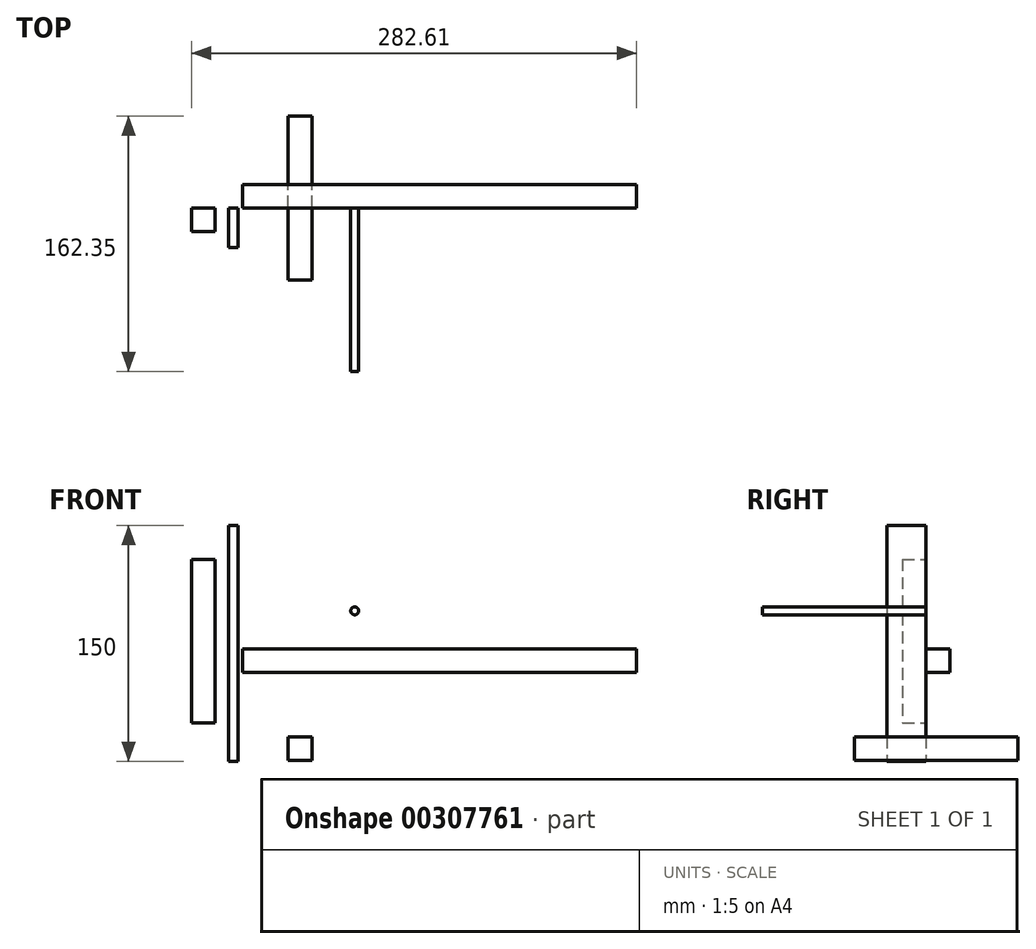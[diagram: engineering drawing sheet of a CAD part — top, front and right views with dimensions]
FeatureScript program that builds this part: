
annotation { "Feature Type Name" : "Feature", "Feature Type Description" : "" }
export const myFeature = defineFeature(function(context is Context, id is Id, definition is map)
    precondition{}
    {
        {
            var Q0;
            Q0=qCreatedBy(makeId("Top.planeOp"),FACE);
            var sketch = newSketch(context, id + "F0", { "sketchPlane" : qUnion([Q0])});
            skLineSegment(sketch, "E0.bottom", {"start": v(-28.87, 15) * mm, "end": v(221.13, 15) * mm});
            skLineSegment(sketch, "E0.top", {"start": v(-28.87, 0) * mm, "end": v(221.13, 0) * mm});
            skLineSegment(sketch, "E0.left", {"start": v(-28.87, 15) * mm, "end": v(-28.87, 0) * mm});
            skLineSegment(sketch, "E0.right", {"start": v(221.13, 15) * mm, "end": v(221.13, 0) * mm});
            skSolve(sketch);
        }
        {
            var Q0;
            Q0 = qSketchRegion(id + "F0", true);
            extrude(context, id + "F1", {"entities" : qUnion([Q0]), "depth" : 15 * mm});
        }
        {
            var Q0;
            Q0=qCreatedBy(makeId("Right.planeOp"),FACE);
            var sketch = newSketch(context, id + "F2", { "sketchPlane" : qUnion([Q0])});
            skLineSegment(sketch, "E1.bottom", {"start": v(-45.65, -40.85) * mm, "end": v(58.35, -40.85) * mm});
            skLineSegment(sketch, "E1.top", {"start": v(-45.65, -55.85) * mm, "end": v(58.35, -55.85) * mm});
            skLineSegment(sketch, "E1.left", {"start": v(-45.65, -40.85) * mm, "end": v(-45.65, -55.85) * mm});
            skLineSegment(sketch, "E1.right", {"start": v(58.35, -40.85) * mm, "end": v(58.35, -55.85) * mm});
            skSolve(sketch);
        }
        {
            var Q0;
            Q0 = qSketchRegion(id + "F2", true);
            extrude(context, id + "F3", {"entities" : qUnion([Q0]), "depth" : 15 * mm});
        }
        {
            var Q0;
            Q0=qCreatedBy(makeId("Front.planeOp"),FACE);
            var sketch = newSketch(context, id + "F4", { "sketchPlane" : qUnion([Q0])});
            skLineSegment(sketch, "E2.bottom", {"start": v(-61.48, 71.86) * mm, "end": v(-46.48, 71.86) * mm});
            skLineSegment(sketch, "E2.top", {"start": v(-61.48, -32.14) * mm, "end": v(-46.48, -32.14) * mm});
            skLineSegment(sketch, "E2.left", {"start": v(-61.48, 71.86) * mm, "end": v(-61.48, -32.14) * mm});
            skLineSegment(sketch, "E2.right", {"start": v(-46.48, 71.86) * mm, "end": v(-46.48, -32.14) * mm});
            skSolve(sketch);
        }
        {
            var Q0;
            Q0 = qSketchRegion(id + "F4", true);
            extrude(context, id + "F5", {"entities" : qUnion([Q0]), "depth" : 15 * mm});
        }
        {
            var Q0;
            Q0=qCreatedBy(makeId("Front.planeOp"),FACE);
            var sketch = newSketch(context, id + "F6", { "sketchPlane" : qUnion([Q0])});
            skCircle(sketch, "E3", {"center": v(42.21, 39.08) * mm, "radius": 2.5 * mm});
            skSolve(sketch);
        }
        {
            var Q0;
            Q0 = qSketchRegion(id + "F6", true);
            extrude(context, id + "F7", {"entities" : qUnion([Q0]), "depth" : 104 * mm});
        }
        {
            var Q0;
            Q0=qCreatedBy(makeId("Front.planeOp"),FACE);
            var sketch = newSketch(context, id + "F8", { "sketchPlane" : qUnion([Q0])});
            skLineSegment(sketch, "E4.bottom", {"start": v(-31.91, 93.47) * mm, "end": v(-37.91, 93.47) * mm});
            skLineSegment(sketch, "E4.top", {"start": v(-31.91, -56.53) * mm, "end": v(-37.91, -56.53) * mm});
            skLineSegment(sketch, "E4.left", {"start": v(-31.91, 93.47) * mm, "end": v(-31.91, -56.53) * mm});
            skLineSegment(sketch, "E4.right", {"start": v(-37.91, 93.47) * mm, "end": v(-37.91, -56.53) * mm});
            skSolve(sketch);
        }
        {
            var Q0;
            Q0 = qSketchRegion(id + "F8", true);
            extrude(context, id + "F9", {"entities" : qUnion([Q0]), "depth" : 25 * mm});
        }
    });
